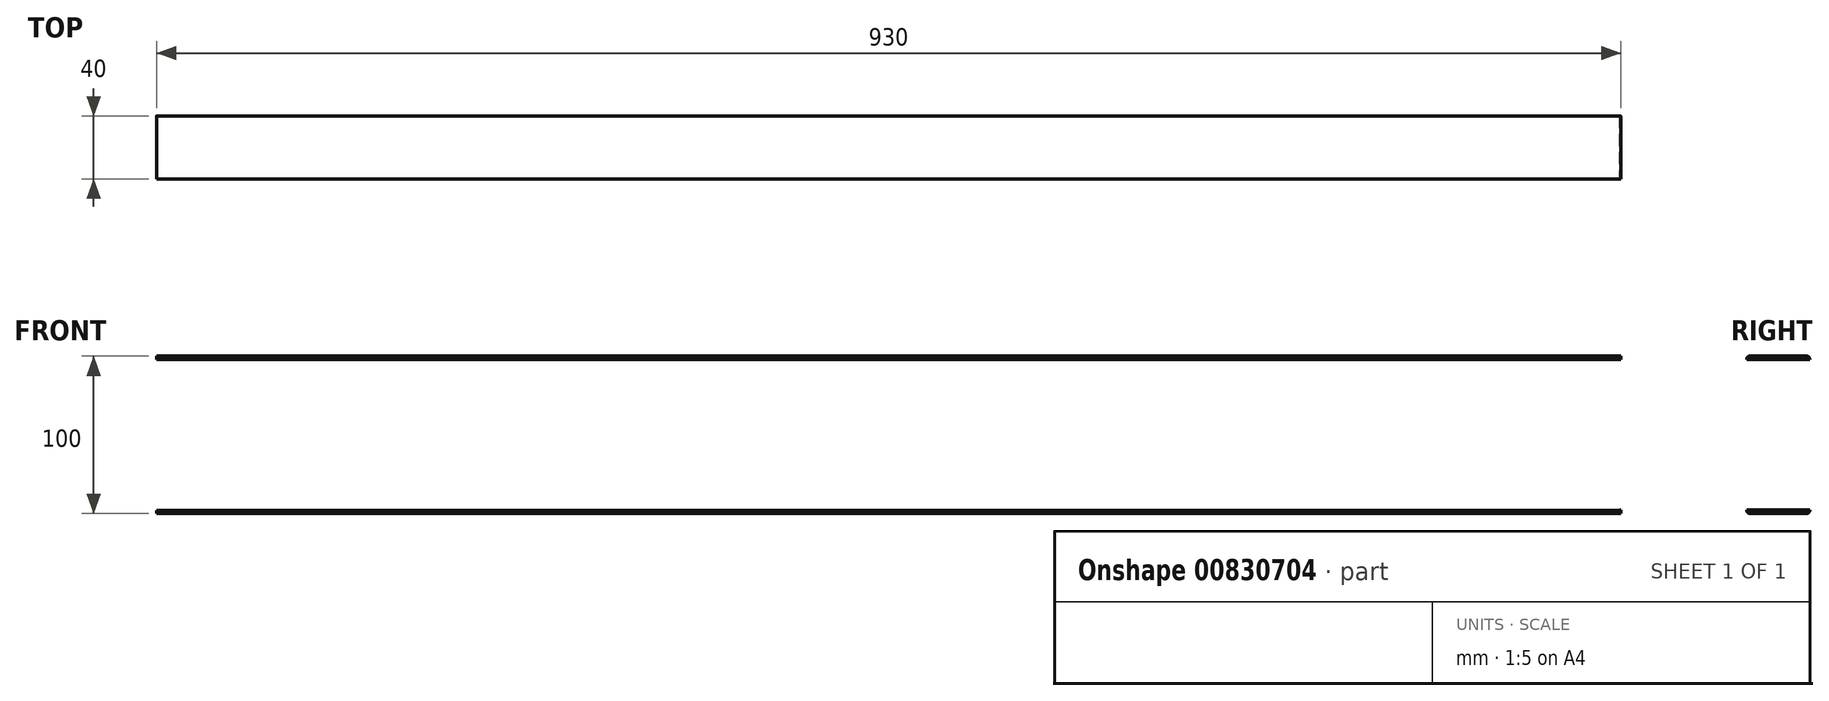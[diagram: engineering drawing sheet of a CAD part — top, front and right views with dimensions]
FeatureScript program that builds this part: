
annotation { "Feature Type Name" : "Feature", "Feature Type Description" : "" }
export const myFeature = defineFeature(function(context is Context, id is Id, definition is map)
    precondition{}
    {
        {
            assignVariable(context, id + "F0", {"name" : "TubeHeight", "anyValue" : 40});
        }
        {
            assignVariable(context, id + "F1", {"name" : "TubeWidth", "anyValue" : 100});
        }
        {
            assignVariable(context, id + "F2", {"name" : "ScissorLength", "anyValue" : 1000});
        }
        {
            var Q0;
            Q0=qCreatedBy(makeId("Right.planeOp"),FACE);
            var sketch = newSketch(context, id + "F3", { "sketchPlane" : qUnion([Q0])});
            skPoint(sketch, "E0.middle", {"position": v(0, 0) * mm});
            skLineSegment(sketch, "E1.bottom", {"start": v(-2.3, -86.5) * mm, "end": v(33.7, -86.5) * mm});
            skLineSegment(sketch, "E1.top", {"start": v(-2.3, 13.5) * mm, "end": v(33.7, 13.5) * mm});
            skLineSegment(sketch, "E1.left", {"start": v(-4.3, -84.5) * mm, "end": v(-4.3, 11.5) * mm});
            skLineSegment(sketch, "E1.right", {"start": v(35.7, -84.5) * mm, "end": v(35.7, 11.5) * mm});
            skPoint(sketch, "E2.visualSharp", {"position": v(-4.3, 13.5) * mm});
            skArc(sketch, "E2.filletArc", {"start": v(-2.3, 13.5) * mm, "mid": v(-3.7, 12.91) * mm, "end": v(-4.3, 11.5) * mm});
            skPoint(sketch, "E3.visualSharp", {"position": v(35.7, 13.5) * mm});
            skArc(sketch, "E3.filletArc", {"start": v(35.7, 11.5) * mm, "mid": v(35.12, 12.91) * mm, "end": v(33.7, 13.5) * mm});
            skPoint(sketch, "E4.visualSharp", {"position": v(35.7, -86.5) * mm});
            skArc(sketch, "E4.filletArc", {"start": v(33.7, -86.5) * mm, "mid": v(35.12, -85.91) * mm, "end": v(35.7, -84.5) * mm});
            skPoint(sketch, "E5.visualSharp", {"position": v(-4.3, -86.5) * mm});
            skArc(sketch, "E5.filletArc", {"start": v(-4.3, -84.5) * mm, "mid": v(-3.7, -85.91) * mm, "end": v(-2.3, -86.5) * mm});
            skLineSegment(sketch, "E6.0", {"start": v(-2.3, 11.5) * mm, "end": v(-2.3, 11.5) * mm});
            skLineSegment(sketch, "E6.2", {"start": v(-2.3, -84.5) * mm, "end": v(-2.3, -84.5) * mm});
            skLineSegment(sketch, "E6.4", {"start": v(33.7, -84.5) * mm, "end": v(33.7, -84.5) * mm});
            skLineSegment(sketch, "E6.7", {"start": v(33.7, 11.5) * mm, "end": v(33.7, 11.5) * mm});
            skLineSegment(sketch, "E7.0", {"start": v(32.7, -83.5) * mm, "end": v(32.7, 10.5) * mm});
            skLineSegment(sketch, "E7.1", {"start": v(-1.3, -83.5) * mm, "end": v(32.7, -83.5) * mm});
            skLineSegment(sketch, "E7.2", {"start": v(-1.3, -83.5) * mm, "end": v(-1.3, 10.5) * mm});
            skLineSegment(sketch, "E7.3", {"start": v(-1.3, 10.5) * mm, "end": v(32.7, 10.5) * mm});
            skSolve(sketch);
        }
        {
            var Q0;
            Q0=makeQuery(id+"F3.imprint","IMPRINT",FACE,{"disambiguationData":[TD([[makeQuery(id+"F3.imprint","IMPRINT",EDGE,{"derivedFrom":sQuery(id+"F3.wireOp",EDGE,"E1.bottom")}),1.0]])]});
            extrude(context, id + "F4", {"entities" : qUnion([Q0]), "endBound" : BoundingType.SYMMETRIC, "depth" : (getVariable(context, 'ScissorLength')) * mm, "hasOffset" : true, "offsetDistance" : 1000 * mm});
        }
        {
            var Q0;
            Q0=makeQuery(id+"F4.opExtrude","SWEPT_FACE",FACE,{"disambiguationData":[OSD([sQuery(id+"F3.wireOp",EDGE,"E1.left")])]});
            var sketch = newSketch(context, id + "F5", { "sketchPlane" : qUnion([Q0])});
            skPoint(sketch, "E8", {"position": v(0, -36.22) * mm});
            skPoint(sketch, "E9.centerSnap0", {"position": v(500, -36.5) * mm});
            skCircle(sketch, "E10.MirrorC", {"center": v(450, -36.22) * mm, "radius": 16.43 * mm, "construction": true});
            skPoint(sketch, "E11.centerSnap0", {"position": v(-500, -36.5) * mm});
            skArc(sketch, "E12", {"start": v(-453.18, 13.4) * mm, "mid": v(-499.97, -38.34) * mm, "end": v(-449.5, -86.5) * mm});
            skPoint(sketch, "E12.second.point", {"position": v(-400, -36.5) * mm});
            skPoint(sketch, "E12.third.point", {"position": v(-453.18, 13.4) * mm});
            skPoint(sketch, "E13", {"position": v(-449.5, -86.5) * mm});
            skArc(sketch, "E14.MirrorCS", {"start": v(453.18, 13.4) * mm, "mid": v(499.97, -38.34) * mm, "end": v(449.5, -86.5) * mm});
            skSolve(sketch);
        }
        {
            var Q0;
            Q0=sQuery(id+"F5.wireOp",VERTEX,"gL0Hj35o-Ipak-IrFQ-axua-rWeWUbhPRuIx.center");
            var Q1;
            Q1=sQuery(id+"F5.wireOp",VERTEX,"E10.MirrorC.center");
            var Q2;
            Q2=sQuery(id+"F5.wireOp",VERTEX,"E8");
            var Q3;
            Q3=sQuery(id+"F5.wireOp",VERTEX,"E12.center");
            var Q4;
            Q4=makeQuery(id+"F4.opExtrude","SWEPT_BODY",BODY,{"disambiguationData":[OSD([sQuery(id+"F3.wireOp",EDGE,"E1.bottom"),sQuery(id+"F3.wireOp",EDGE,"E1.top"),sQuery(id+"F3.wireOp",EDGE,"E1.left"),sQuery(id+"F3.wireOp",EDGE,"E1.right"),sQuery(id+"F3.wireOp",EDGE,"E2.filletArc"),sQuery(id+"F3.wireOp",EDGE,"E3.filletArc"),sQuery(id+"F3.wireOp",EDGE,"E4.filletArc"),sQuery(id+"F3.wireOp",EDGE,"E5.filletArc"),sQuery(id+"F3.wireOp",EDGE,"E7.0"),sQuery(id+"F3.wireOp",EDGE,"E7.1"),sQuery(id+"F3.wireOp",EDGE,"E7.2"),sQuery(id+"F3.wireOp",EDGE,"E7.3")])]});
            hole(context, id + "F6", {"style" : HoleStyle.SIMPLE, "endStyle" : HoleEndStyle.BLIND, "holeDiameter" : 12 * mm, "majorDiameter" : 5 * mm, "holeDepth" : 40 * mm, "isTappedThrough" : true, "tappedDepth" : 12 * mm, "tapClearance" : 3, "startFromSketch" : true, "locations" : qUnion([Q0, Q1, Q2, Q3]), "scope" : qUnion([Q4])});
        }
        {
            var Q0;
            {var subQ0=sQuery(id+"F5.wireOp",EDGE,"E12");var subQ1=sQuery(id+"F3.wireOp",EDGE,"E1.left");var subQ4=makeQuery(id+"F4.opExtrude","CAP_EDGE",EDGE,{"disambiguationData":[OSD([subQ1])],"isStart":true});var subQ5=makeQuery(id+"F5.imprint","INTERSECT",VERTEX,{"derivedFrom":[subQ4,subQ0]});Q0=makeQuery(id+"F5.imprint","IMPRINT",FACE,{"disambiguationData":[TD([[makeQuery(id+"F5.imprint","IMPRINT",EDGE,{"disambiguationData":[TD([[subQ5,1.0]])],"derivedFrom":subQ0}),-1.0]])]});}
            var Q1;
            {var subQ0=sQuery(id+"F5.wireOp",EDGE,"E12");var subQ1=sQuery(id+"F3.wireOp",EDGE,"E1.left");var subQ2=makeQuery(id+"F4.opExtrude","CAP_EDGE",EDGE,{"disambiguationData":[OSD([subQ1])],"isStart":true});var subQ3=makeQuery(id+"F5.imprint","INTERSECT",VERTEX,{"derivedFrom":[subQ2,subQ0]});Q1=makeQuery(id+"F5.imprint","IMPRINT",FACE,{"disambiguationData":[TD([[makeQuery(id+"F5.imprint","IMPRINT",EDGE,{"disambiguationData":[TD([[subQ3,-1.0]])],"derivedFrom":subQ0}),-1.0]])]});}
            var Q2;
            {var subQ0=sQuery(id+"F5.wireOp",EDGE,"E14.MirrorCS");var subQ1=sQuery(id+"F3.wireOp",EDGE,"E1.left");var subQ4=makeQuery(id+"F4.opExtrude","CAP_EDGE",EDGE,{"disambiguationData":[OSD([subQ1])],"isStart":false});var subQ5=makeQuery(id+"F5.imprint","INTERSECT",VERTEX,{"derivedFrom":[subQ4,subQ0]});Q2=makeQuery(id+"F5.imprint","IMPRINT",FACE,{"disambiguationData":[TD([[makeQuery(id+"F5.imprint","IMPRINT",EDGE,{"disambiguationData":[TD([[subQ5,1.0]])],"derivedFrom":subQ0}),1.0]])]});}
            var Q3;
            {var subQ0=sQuery(id+"F5.wireOp",EDGE,"E14.MirrorCS");var subQ1=sQuery(id+"F3.wireOp",EDGE,"E1.left");var subQ4=makeQuery(id+"F4.opExtrude","CAP_EDGE",EDGE,{"disambiguationData":[OSD([subQ1])],"isStart":false});var subQ5=makeQuery(id+"F5.imprint","INTERSECT",VERTEX,{"derivedFrom":[subQ4,subQ0]});Q3=makeQuery(id+"F5.imprint","IMPRINT",FACE,{"disambiguationData":[TD([[makeQuery(id+"F5.imprint","IMPRINT",EDGE,{"disambiguationData":[TD([[subQ5,-1.0]])],"derivedFrom":subQ0}),1.0]])]});}
            var Q4;
            Q4=sQuery(id+"F5.wireOp",EDGE,"giCMITpL-clwF-rWN8-tJVd-up4GtD5okeqH");
            extrude(context, id + "F7", {"entities" : qUnion([Q0, Q1, Q2, Q3]), "operationType" : NewBodyOperationType.REMOVE, "surfaceEntities" : qUnion([Q4]), "depth" : -(getVariable(context, 'TubeHeight')) * mm, "offsetDistance" : 25 * mm});
        }
        {
            var Q0;
            {var subQ0=sQuery(id+"F3.wireOp",EDGE,"E1.top");var subQ1=sQuery(id+"F3.wireOp",EDGE,"E2.filletArc");var subQ2=sQuery(id+"F3.wireOp",EDGE,"E1.left");var subQ3=sQuery(id+"F3.wireOp",EDGE,"E3.filletArc");Q0=makeQuery(id+"F7.boolean.opBoolean","SPLIT",FACE,{"disambiguationData":[TD([makeQuery(id+"F4.opExtrude","SWEPT_FACE",FACE,{"disambiguationData":[OSD([subQ0])]})])],"derivedFrom":makeQuery(id+"F4.opExtrude","CAP_FACE",FACE,{"disambiguationData":[OSD([sQuery(id+"F3.wireOp",EDGE,"E1.bottom"),subQ0,subQ2,sQuery(id+"F3.wireOp",EDGE,"E1.right"),subQ1,subQ3,sQuery(id+"F3.wireOp",EDGE,"E4.filletArc"),sQuery(id+"F3.wireOp",EDGE,"E5.filletArc"),sQuery(id+"F3.wireOp",EDGE,"E7.0"),sQuery(id+"F3.wireOp",EDGE,"E7.1"),sQuery(id+"F3.wireOp",EDGE,"E7.2"),sQuery(id+"F3.wireOp",EDGE,"E7.3")])],"isStart":true})});}
            var Q1;
            {var subQ0=sQuery(id+"F3.wireOp",EDGE,"E1.bottom");var subQ1=sQuery(id+"F3.wireOp",EDGE,"E4.filletArc");var subQ2=sQuery(id+"F3.wireOp",EDGE,"E5.filletArc");var subQ3=sQuery(id+"F3.wireOp",EDGE,"E1.left");Q1=makeQuery(id+"F7.boolean.opBoolean","SPLIT",FACE,{"disambiguationData":[TD([makeQuery(id+"F4.opExtrude","SWEPT_FACE",FACE,{"disambiguationData":[OSD([subQ0])]})])],"derivedFrom":makeQuery(id+"F4.opExtrude","CAP_FACE",FACE,{"disambiguationData":[OSD([subQ0,sQuery(id+"F3.wireOp",EDGE,"E1.top"),subQ3,sQuery(id+"F3.wireOp",EDGE,"E1.right"),sQuery(id+"F3.wireOp",EDGE,"E2.filletArc"),sQuery(id+"F3.wireOp",EDGE,"E3.filletArc"),subQ1,subQ2,sQuery(id+"F3.wireOp",EDGE,"E7.0"),sQuery(id+"F3.wireOp",EDGE,"E7.1"),sQuery(id+"F3.wireOp",EDGE,"E7.2"),sQuery(id+"F3.wireOp",EDGE,"E7.3")])],"isStart":true})});}
            var Q2;
            Q2=sQuery(id+"F3.wireOp",EDGE,"E3.filletArc");
            var Q3;
            Q3=sQuery(id+"F3.wireOp",EDGE,"E1.top");
            var Q4;
            Q4=sQuery(id+"F3.wireOp",EDGE,"E2.filletArc");
            extrude(context, id + "F8", {"entities" : qUnion([Q0, Q1]), "operationType" : NewBodyOperationType.REMOVE, "surfaceEntities" : qUnion([Q2, Q3, Q4]), "oppositeDirection" : true, "depth" : (getVariable(context, 'TubeWidth') / 2 - 15) * mm, "offsetDistance" : 25 * mm});
        }
        {
            var Q0;
            {var subQ0=sQuery(id+"F3.wireOp",EDGE,"E1.bottom");var subQ1=sQuery(id+"F3.wireOp",EDGE,"E4.filletArc");var subQ2=sQuery(id+"F3.wireOp",EDGE,"E5.filletArc");var subQ3=sQuery(id+"F3.wireOp",EDGE,"E1.left");Q0=makeQuery(id+"F7.boolean.opBoolean","SPLIT",FACE,{"disambiguationData":[TD([makeQuery(id+"F4.opExtrude","SWEPT_FACE",FACE,{"disambiguationData":[OSD([subQ0])]})])],"derivedFrom":makeQuery(id+"F4.opExtrude","CAP_FACE",FACE,{"disambiguationData":[OSD([subQ0,sQuery(id+"F3.wireOp",EDGE,"E1.top"),subQ3,sQuery(id+"F3.wireOp",EDGE,"E1.right"),sQuery(id+"F3.wireOp",EDGE,"E2.filletArc"),sQuery(id+"F3.wireOp",EDGE,"E3.filletArc"),subQ1,subQ2,sQuery(id+"F3.wireOp",EDGE,"E7.0"),sQuery(id+"F3.wireOp",EDGE,"E7.1"),sQuery(id+"F3.wireOp",EDGE,"E7.2"),sQuery(id+"F3.wireOp",EDGE,"E7.3")])],"isStart":false})});}
            var Q1;
            {var subQ0=sQuery(id+"F3.wireOp",EDGE,"E1.top");var subQ1=sQuery(id+"F3.wireOp",EDGE,"E2.filletArc");var subQ2=sQuery(id+"F3.wireOp",EDGE,"E1.left");var subQ4=sQuery(id+"F3.wireOp",EDGE,"E3.filletArc");Q1=makeQuery(id+"F7.boolean.opBoolean","SPLIT",FACE,{"disambiguationData":[TD([makeQuery(id+"F4.opExtrude","SWEPT_FACE",FACE,{"disambiguationData":[OSD([subQ0])]})])],"derivedFrom":makeQuery(id+"F4.opExtrude","CAP_FACE",FACE,{"disambiguationData":[OSD([sQuery(id+"F3.wireOp",EDGE,"E1.bottom"),subQ0,subQ2,sQuery(id+"F3.wireOp",EDGE,"E1.right"),subQ1,subQ4,sQuery(id+"F3.wireOp",EDGE,"E4.filletArc"),sQuery(id+"F3.wireOp",EDGE,"E5.filletArc"),sQuery(id+"F3.wireOp",EDGE,"E7.0"),sQuery(id+"F3.wireOp",EDGE,"E7.1"),sQuery(id+"F3.wireOp",EDGE,"E7.2"),sQuery(id+"F3.wireOp",EDGE,"E7.3")])],"isStart":false})});}
            extrude(context, id + "F9", {"entities" : qUnion([Q0, Q1]), "operationType" : NewBodyOperationType.REMOVE, "oppositeDirection" : true, "depth" : (getVariable(context, 'TubeWidth') / 2 - 15) * mm, "offsetDistance" : 25 * mm});
        }
    });
